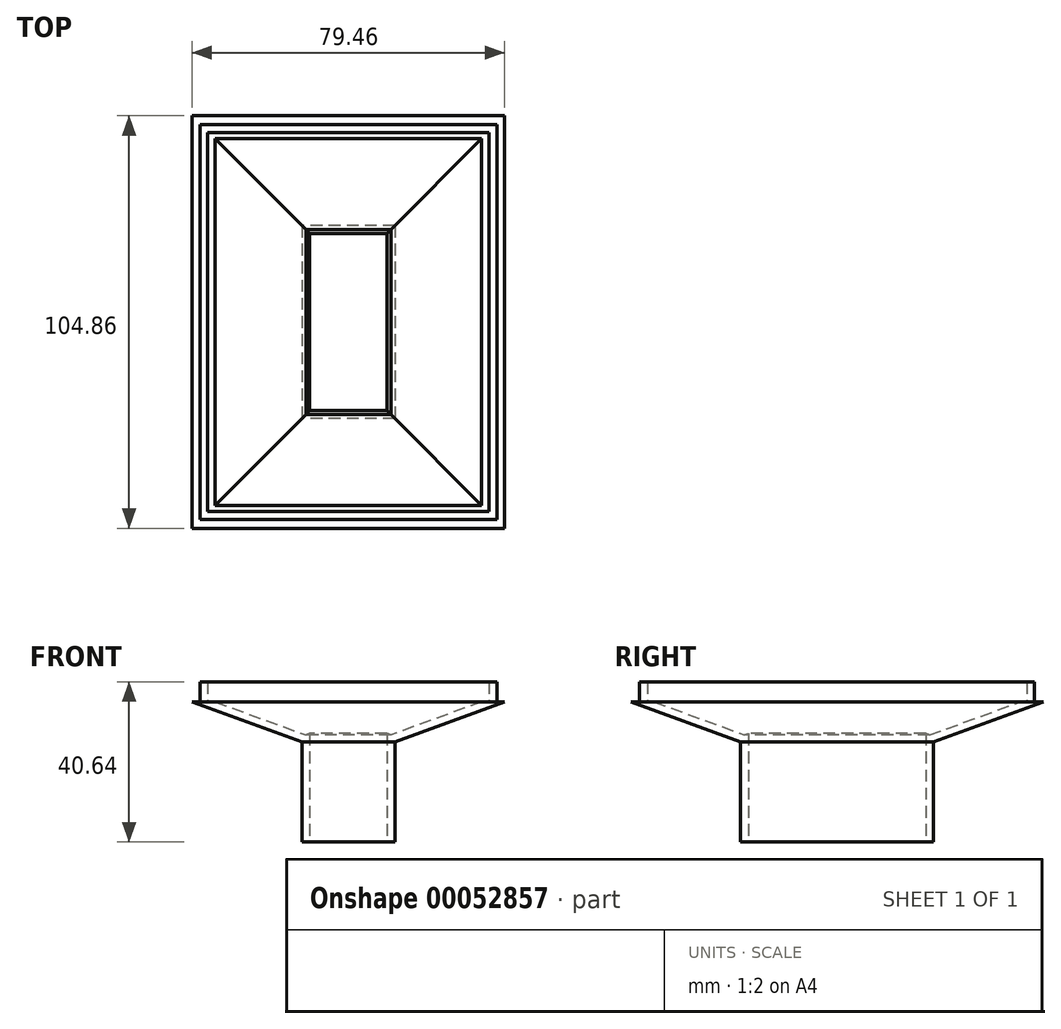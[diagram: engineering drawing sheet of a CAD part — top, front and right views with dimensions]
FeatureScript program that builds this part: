
annotation { "Feature Type Name" : "Feature", "Feature Type Description" : "" }
export const myFeature = defineFeature(function(context is Context, id is Id, definition is map)
    precondition{}
    {
        {
            var Q0;
            Q0=qCreatedBy(makeId("Top.planeOp"),FACE);
            var sketch = newSketch(context, id + "F0", { "sketchPlane" : qUnion([Q0])});
            skLineSegment(sketch, "E0.bottom", {"start": v(11.81, 24.51) * mm, "end": v(-11.81, 24.51) * mm});
            skLineSegment(sketch, "E0.top", {"start": v(11.81, -24.51) * mm, "end": v(-11.81, -24.51) * mm});
            skLineSegment(sketch, "E0.left", {"start": v(11.81, 24.51) * mm, "end": v(11.81, -24.51) * mm});
            skLineSegment(sketch, "E0.right", {"start": v(-11.81, 24.51) * mm, "end": v(-11.81, -24.51) * mm});
            skPoint(sketch, "E0.middle", {"position": v(0, 0) * mm});
            skLineSegment(sketch, "E1.bottom", {"start": v(9.81, 22.51) * mm, "end": v(-9.81, 22.51) * mm});
            skLineSegment(sketch, "E1.top", {"start": v(9.81, -22.51) * mm, "end": v(-9.81, -22.51) * mm});
            skLineSegment(sketch, "E1.left", {"start": v(9.81, 22.51) * mm, "end": v(9.81, -22.51) * mm});
            skLineSegment(sketch, "E1.right", {"start": v(-9.81, 22.51) * mm, "end": v(-9.81, -22.51) * mm});
            skSolve(sketch);
        }
        {
            var Q0;
            Q0=makeQuery(id+"F0.imprint","IMPRINT",FACE,{"disambiguationData":[TD([[makeQuery(id+"F0.imprint","IMPRINT",EDGE,{"derivedFrom":sQuery(id+"F0.wireOp",EDGE,"E0.bottom")}),1.0]])]});
            extrude(context, id + "F1", {"entities" : qUnion([Q0]), "depth" : 25.4 * mm});
        }
        {
            var Q0;
            Q0=makeQuery(id+"F1.opExtrude","CAP_FACE",FACE,{"disambiguationData":[OSD([sQuery(id+"F0.wireOp",EDGE,"E0.bottom"),sQuery(id+"F0.wireOp",EDGE,"E0.top"),sQuery(id+"F0.wireOp",EDGE,"E0.left"),sQuery(id+"F0.wireOp",EDGE,"E0.right"),sQuery(id+"F0.wireOp",EDGE,"E1.bottom"),sQuery(id+"F0.wireOp",EDGE,"E1.top"),sQuery(id+"F0.wireOp",EDGE,"E1.left"),sQuery(id+"F0.wireOp",EDGE,"E1.right")])],"isStart":false});
            extrude(context, id + "F2", {"entities" : qUnion([Q0]), "operationType" : NewBodyOperationType.ADD, "depth" : 10.16 * mm, "hasDraft" : true, "draftAngle" : 70 * degree});
        }
        {
            var Q0;
            Q0=makeQuery(id+"F2.opExtrude","CAP_FACE",FACE,{"disambiguationData":[OSD([sQuery(id+"F0.wireOp",EDGE,"E0.bottom"),sQuery(id+"F0.wireOp",EDGE,"E0.top"),sQuery(id+"F0.wireOp",EDGE,"E0.left"),sQuery(id+"F0.wireOp",EDGE,"E0.right"),sQuery(id+"F0.wireOp",EDGE,"E1.bottom"),sQuery(id+"F0.wireOp",EDGE,"E1.top"),sQuery(id+"F0.wireOp",EDGE,"E1.left"),sQuery(id+"F0.wireOp",EDGE,"E1.right")])],"isStart":false});
            shell(context, id + "F3", {"entities" : qUnion([Q0]), "thickness" : 2 * mm});
        }
        {
            var Q0;
            Q0=makeQuery(id+"F1.opExtrude","CAP_FACE",FACE,{"disambiguationData":[OSD([sQuery(id+"F0.wireOp",EDGE,"E0.bottom"),sQuery(id+"F0.wireOp",EDGE,"E0.top"),sQuery(id+"F0.wireOp",EDGE,"E0.left"),sQuery(id+"F0.wireOp",EDGE,"E0.right"),sQuery(id+"F0.wireOp",EDGE,"E1.bottom"),sQuery(id+"F0.wireOp",EDGE,"E1.top"),sQuery(id+"F0.wireOp",EDGE,"E1.left"),sQuery(id+"F0.wireOp",EDGE,"E1.right")])],"isStart":true});
            var sketch = newSketch(context, id + "F4", { "sketchPlane" : qUnion([Q0])});
            skLineSegment(sketch, "E2.bottom", {"start": v(-9.81, 22.51) * mm, "end": v(9.81, 22.51) * mm});
            skLineSegment(sketch, "E2.top", {"start": v(-9.81, -22.51) * mm, "end": v(9.81, -22.51) * mm});
            skLineSegment(sketch, "E2.left", {"start": v(-9.81, 22.51) * mm, "end": v(-9.81, -22.51) * mm});
            skLineSegment(sketch, "E2.right", {"start": v(9.81, 22.51) * mm, "end": v(9.81, -22.51) * mm});
            skPoint(sketch, "E2.middle", {"position": v(0, 0) * mm});
            skSolve(sketch);
        }
        {
            var Q0;
            Q0=makeQuery(id+"F4.imprint","IMPRINT",FACE,{"disambiguationData":[TD([[makeQuery(id+"F4.imprint","IMPRINT",EDGE,{"derivedFrom":sQuery(id+"F4.wireOp",EDGE,"E2.bottom")}),1.0]])]});
            extrude(context, id + "F5", {"entities" : qUnion([Q0]), "operationType" : NewBodyOperationType.REMOVE, "endBound" : BoundingType.THROUGH_ALL, "oppositeDirection" : true, "depth" : 25.4 * mm});
        }
        {
            var Q0;
            Q0=makeQuery(id+"F2.opExtrude","CAP_FACE",FACE,{"disambiguationData":[OSD([sQuery(id+"F0.wireOp",EDGE,"E0.bottom"),sQuery(id+"F0.wireOp",EDGE,"E0.top"),sQuery(id+"F0.wireOp",EDGE,"E0.left"),sQuery(id+"F0.wireOp",EDGE,"E0.right"),sQuery(id+"F0.wireOp",EDGE,"E1.bottom"),sQuery(id+"F0.wireOp",EDGE,"E1.top"),sQuery(id+"F0.wireOp",EDGE,"E1.left"),sQuery(id+"F0.wireOp",EDGE,"E1.right")])],"isStart":false});
            var sketch = newSketch(context, id + "F6", { "sketchPlane" : qUnion([Q0])});
            skLineSegment(sketch, "E3.bottom", {"start": v(35.73, -48.16) * mm, "end": v(-35.73, -48.16) * mm});
            skLineSegment(sketch, "E3.top", {"start": v(35.73, 48.16) * mm, "end": v(-35.73, 48.16) * mm});
            skLineSegment(sketch, "E3.left", {"start": v(35.73, -48.16) * mm, "end": v(35.73, 48.16) * mm});
            skLineSegment(sketch, "E3.right", {"start": v(-35.73, -48.16) * mm, "end": v(-35.73, 48.16) * mm});
            skPoint(sketch, "E3.middle", {"position": v(0, 0) * mm});
            skLineSegment(sketch, "E4.bottom", {"start": v(37.73, -50.16) * mm, "end": v(-37.73, -50.16) * mm});
            skLineSegment(sketch, "E4.top", {"start": v(37.73, 50.16) * mm, "end": v(-37.73, 50.16) * mm});
            skLineSegment(sketch, "E4.left", {"start": v(37.73, -50.16) * mm, "end": v(37.73, 50.16) * mm});
            skLineSegment(sketch, "E4.right", {"start": v(-37.73, -50.16) * mm, "end": v(-37.73, 50.16) * mm});
            skSolve(sketch);
        }
        {
            var Q0;
            Q0=makeQuery(id+"F6.imprint","IMPRINT",FACE,{"disambiguationData":[TD([[makeQuery(id+"F6.imprint","IMPRINT",EDGE,{"derivedFrom":sQuery(id+"F6.wireOp",EDGE,"E3.bottom")}),1.0]])]});
            extrude(context, id + "F7", {"entities" : qUnion([Q0]), "operationType" : NewBodyOperationType.ADD, "depth" : 5.08 * mm});
        }
    });
